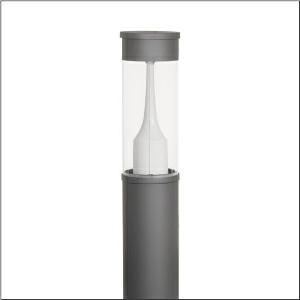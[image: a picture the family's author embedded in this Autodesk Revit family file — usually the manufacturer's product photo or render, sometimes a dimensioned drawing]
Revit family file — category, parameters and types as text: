
# Revit family: city-light_400_iq___st1_2a_5xa5305kf14h_7e7c
name_source: partatom
category: Lighting Fixtures
units: mm (PartAtom-declared; Revit-internal decimal feet)

## family parameters
Cut with Voids When Loaded = No
Host = Face
Light Source = No
Part Type = Normal
Room Calculation Point = No
Round Connector Dimension = Use Diameter
Shared = No

## types (1)
- --- (1 x LED, 1540 lm, 10 W, 4000K)
    Apparent Load = 10 VA
    CIE Flux Codes = 22 61 93 96 100
    Color Rendering = 70
    Color Temperature = 4000K
    Default Elevation = 1800 mm
    Description = City-Light 400 iQ, light pillar, Module 540 iQ-SR, primary light control with 3 zone facetted reflector, of plastic, silver coated, highly specular, structured, primary optical cover: cover, of PMMA, transparent, partly coated, light distribution: ST1.2a, primary light characteristic: asymmetric, LED, High Power LED, rated luminous flux: 1.540lm, luminous efficacy: 154lm/W, light colour: 740, colour temperature: 4000K, control gear: ECG iQ, control: presetting dimming logarithmic, Street-Remote, Auto-Match, Temp-Guard, Lumen-Switch, Night-Set, Smart-Wire, Light-Fading, Desk-Remote (wireless, voltage-free reading and setting of iQ features in the workshop via application-optimized NFC function/RFID function), optimised constant luminous flux control (CLO 2.0), with terminal, 6-pole, max. 2.5mm², mains connection: 230..240V, AC, 50/60Hz, start of lifetime: 10W, end of service life: 10W, reduction: 5W, luminaire housing, cylindrical, of extruded aluminium section, coated, Siteco® metallic grey (DB 702S), length: 4.694mm, diameter: 200mm, Module 540 iQ-SR, traffic white (RAL 9016), equipment: standard, protection rating (complete): IP65, insulation class (complete): insulation class II (safety insulation), certification: CE, ENEC, VDE, packaging unit: 1 piece

Light Distribution: ST1.2a
    Height = 500 mm
    Lamp = 1 x LED
    Lamp Light Flux = 1540 lm
    Lamp Power = 10 W
    Lamp count = 1
    Length = 200 mm  [stored 0.656168 ft]
    Luminous efficacy = 154 lm/W
    Manufacturer = Siteco
    ModVariant = No
    Model = 5XA5305KF14H
    Mounting Place = Floor
    Mounting Type = Freestanding
    Number of Poles = 1
    OnlyDefault = Yes
    Power Factor = 1
    Product Name = City-Light 400 iQ | ST1.2a
    Product group = light pillar
    ProductGroupID = 1303
    Protection Class = Protection class II
    Protection Degree = IP 65
    RLX_Detail_Level = 1
    RLX_Emergency_Light_Flux = 0 lm
    RLX_Emergency_Type = 0
    RLX_Emergency_Type_DB = No
    RlxData = <blob elided: 87421 chars, md5=251f81cd>
    Socket = socket
    Standby Power = 0 W
    System Light Flux = 1540 lm
    System Power = 10 W
    Type Comments = factory setting: luminous flux: 100 % | dim-lin: 254 | 401 mA
    Type Image = l_1006914.jpg
    URL = http://relux.com
    VarID = @adj_091397
    Voltage = 0 V
    Weight = 0.00 kg
    Width = 0 mm  [stored 0 ft]

note: [stored X ft] marks values corroborated as IEEE doubles in the binary element streams (Revit-internal decimal feet)

## geometry (parser evidence)
native form markers: Blend x4, Sweep x10
no freeform markers — native parametric forms only
